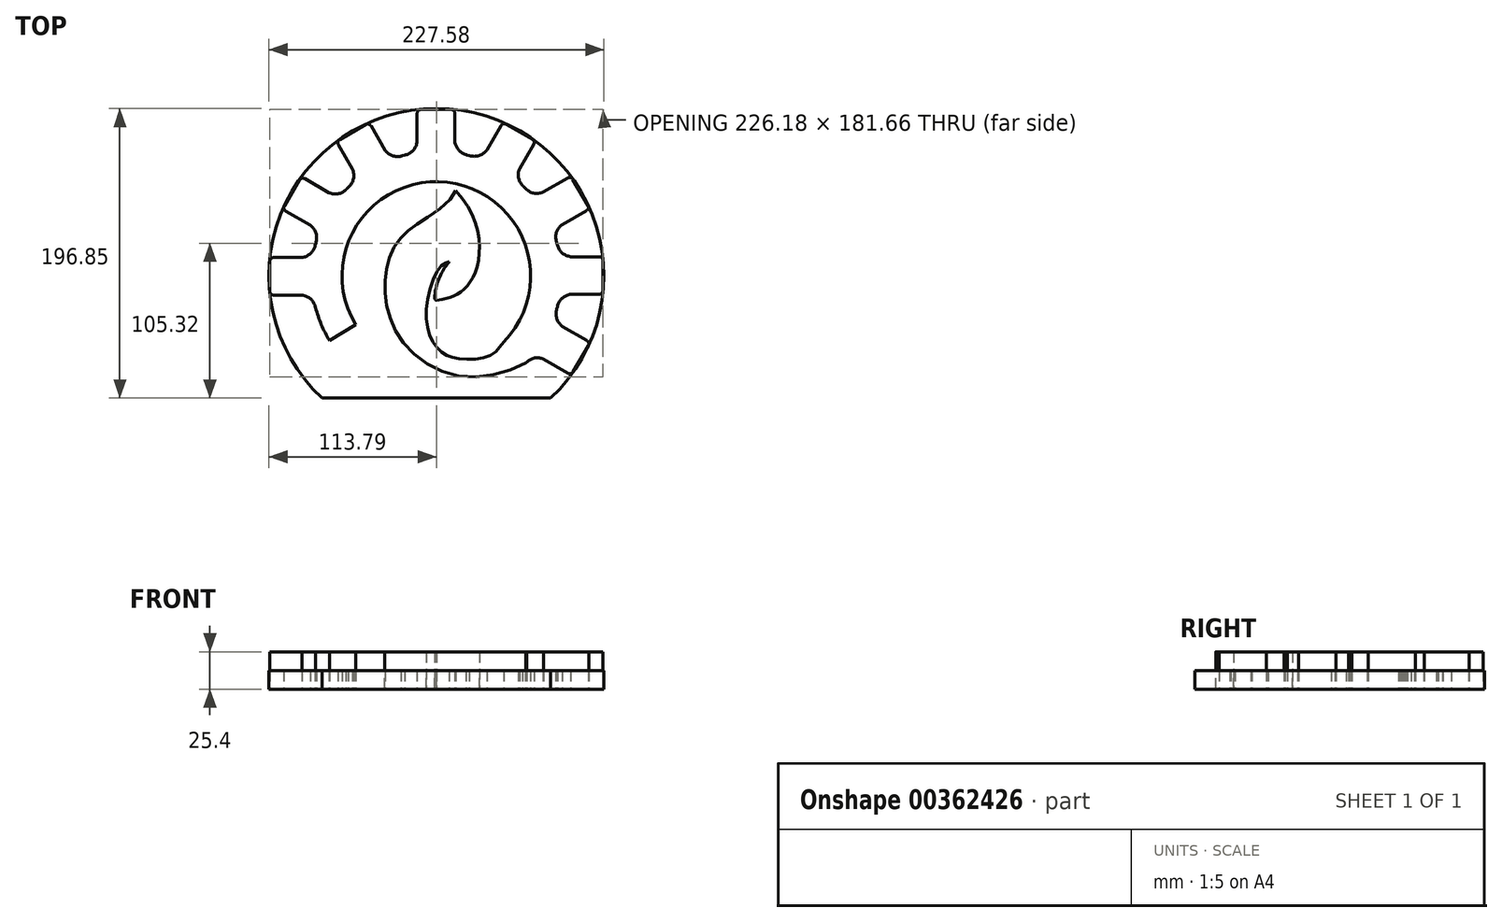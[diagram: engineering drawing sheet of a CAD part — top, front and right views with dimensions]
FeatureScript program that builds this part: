
annotation { "Feature Type Name" : "Feature", "Feature Type Description" : "" }
export const myFeature = defineFeature(function(context is Context, id is Id, definition is map)
    precondition{}
    {
        {
            var Q0;
            Q0=qCreatedBy(makeId("Top.planeOp"),FACE);
            var sketch = newSketch(context, id + "F0", { "sketchPlane" : qUnion([Q0])});
            skArc(sketch, "E0", {"start": v(45.83, -44.78) * mm, "mid": v(7.38, 63.65) * mm, "end": v(-54.86, -33.1) * mm});
            skArc(sketch, "E1", {"start": v(60.8, -59.24) * mm, "mid": v(61.11, -58.91) * mm, "end": v(61.43, -58.58) * mm});
            skLineSegment(sketch, "E2", {"start": v(-91.4, -13.07) * mm, "end": v(-110.55, -13.07) * mm});
            skLineSegment(sketch, "E3", {"start": v(-113.1, -10.53) * mm, "end": v(-113.1, 9.96) * mm});
            skLineSegment(sketch, "E4", {"start": v(-110.55, 12.5) * mm, "end": v(-91.4, 12.5) * mm});
            skPoint(sketch, "E5.visualSharp", {"position": v(-113.1, 12.5) * mm});
            skArc(sketch, "E5.filletArc", {"start": v(-110.55, 12.5) * mm, "mid": v(-112.35, 11.76) * mm, "end": v(-113.1, 9.96) * mm});
            skPoint(sketch, "E6.visualSharp", {"position": v(-113.1, -13.07) * mm});
            skArc(sketch, "E6.filletArc", {"start": v(-113.1, -10.53) * mm, "mid": v(-112.35, -12.32) * mm, "end": v(-110.55, -13.07) * mm});
            skArc(sketch, "E7", {"start": v(-91.4, 12.5) * mm, "mid": v(-85.48, 15.23) * mm, "end": v(-82.27, 20.9) * mm});
            skArc(sketch, "E8.MirrorCS", {"start": v(-91.4, -13.07) * mm, "mid": v(-85.34, -15.78) * mm, "end": v(-82.1, -21.58) * mm});
            skPoint(sketch, "E9.start.orphan", {"position": v(-113.1, -0.28) * mm});
            skArc(sketch, "E10.5.0", {"start": v(72.9, -56.53) * mm, "mid": v(66.41, -55.92) * mm, "end": v(60.8, -59.24) * mm});
            skLineSegment(sketch, "E10.5.1", {"start": v(89.49, -66.1) * mm, "end": v(72.9, -56.53) * mm});
            skLineSegment(sketch, "E10.5.2", {"start": v(103.2, -47.43) * mm, "end": v(92.96, -65.18) * mm});
            skLineSegment(sketch, "E10.5.3", {"start": v(85.69, -34.38) * mm, "end": v(102.27, -43.96) * mm});
            skArc(sketch, "E10.5.4", {"start": v(85.69, -34.38) * mm, "mid": v(81.8, -29) * mm, "end": v(81.89, -22.36) * mm});
            skArc(sketch, "E10.5.5", {"start": v(103.2, -47.43) * mm, "mid": v(103.46, -45.5) * mm, "end": v(102.27, -43.96) * mm});
            skArc(sketch, "E10.5.6", {"start": v(89.49, -66.1) * mm, "mid": v(91.42, -66.36) * mm, "end": v(92.96, -65.18) * mm});
            skArc(sketch, "E10.6.0", {"start": v(91.4, -12.5) * mm, "mid": v(85.48, -15.23) * mm, "end": v(82.27, -20.9) * mm});
            skLineSegment(sketch, "E10.6.1", {"start": v(110.55, -12.5) * mm, "end": v(91.4, -12.5) * mm});
            skLineSegment(sketch, "E10.6.2", {"start": v(113.1, 10.53) * mm, "end": v(113.1, -9.96) * mm});
            skLineSegment(sketch, "E10.6.3", {"start": v(91.4, 13.07) * mm, "end": v(110.55, 13.07) * mm});
            skArc(sketch, "E10.6.4", {"start": v(91.4, 13.07) * mm, "mid": v(85.34, 15.78) * mm, "end": v(82.1, 21.58) * mm});
            skArc(sketch, "E10.6.5", {"start": v(113.1, 10.53) * mm, "mid": v(112.35, 12.32) * mm, "end": v(110.55, 13.07) * mm});
            skArc(sketch, "E10.6.6", {"start": v(110.55, -12.5) * mm, "mid": v(112.35, -11.76) * mm, "end": v(113.1, -9.96) * mm});
            skArc(sketch, "E10.7.0", {"start": v(85.41, 34.87) * mm, "mid": v(81.64, 29.55) * mm, "end": v(81.7, 23.03) * mm});
            skLineSegment(sketch, "E10.7.1", {"start": v(102, 44.45) * mm, "end": v(85.41, 34.87) * mm});
            skLineSegment(sketch, "E10.7.2", {"start": v(92.68, 65.66) * mm, "end": v(102.92, 47.92) * mm});
            skLineSegment(sketch, "E10.7.3", {"start": v(72.62, 57.01) * mm, "end": v(89.2, 66.6) * mm});
            skArc(sketch, "E10.7.4", {"start": v(72.62, 57.01) * mm, "mid": v(66.01, 56.34) * mm, "end": v(60.3, 59.74) * mm});
            skArc(sketch, "E10.7.5", {"start": v(92.68, 65.66) * mm, "mid": v(91.14, 66.84) * mm, "end": v(89.2, 66.6) * mm});
            skArc(sketch, "E10.7.6", {"start": v(102, 44.45) * mm, "mid": v(103.18, 45.99) * mm, "end": v(102.92, 47.92) * mm});
            skArc(sketch, "E10.8.0", {"start": v(56.53, 72.9) * mm, "mid": v(55.92, 66.41) * mm, "end": v(59.24, 60.8) * mm});
            skLineSegment(sketch, "E10.8.1", {"start": v(66.1, 89.49) * mm, "end": v(56.53, 72.9) * mm});
            skLineSegment(sketch, "E10.8.2", {"start": v(47.43, 103.2) * mm, "end": v(65.18, 92.96) * mm});
            skLineSegment(sketch, "E10.8.3", {"start": v(34.38, 85.69) * mm, "end": v(43.96, 102.27) * mm});
            skArc(sketch, "E10.8.4", {"start": v(34.38, 85.69) * mm, "mid": v(29, 81.8) * mm, "end": v(22.36, 81.89) * mm});
            skArc(sketch, "E10.8.5", {"start": v(47.43, 103.2) * mm, "mid": v(45.5, 103.46) * mm, "end": v(43.96, 102.27) * mm});
            skArc(sketch, "E10.8.6", {"start": v(66.1, 89.49) * mm, "mid": v(66.36, 91.42) * mm, "end": v(65.18, 92.96) * mm});
            skArc(sketch, "E10.9.0", {"start": v(12.5, 91.4) * mm, "mid": v(15.23, 85.48) * mm, "end": v(20.9, 82.27) * mm});
            skLineSegment(sketch, "E10.9.1", {"start": v(12.5, 110.55) * mm, "end": v(12.5, 91.4) * mm});
            skLineSegment(sketch, "E10.9.2", {"start": v(-10.53, 113.1) * mm, "end": v(9.96, 113.1) * mm});
            skLineSegment(sketch, "E10.9.3", {"start": v(-13.07, 91.4) * mm, "end": v(-13.07, 110.55) * mm});
            skArc(sketch, "E10.9.4", {"start": v(-13.07, 91.4) * mm, "mid": v(-15.78, 85.34) * mm, "end": v(-21.58, 82.1) * mm});
            skArc(sketch, "E10.9.5", {"start": v(-10.53, 113.1) * mm, "mid": v(-12.32, 112.35) * mm, "end": v(-13.07, 110.55) * mm});
            skArc(sketch, "E10.9.6", {"start": v(12.5, 110.55) * mm, "mid": v(11.76, 112.35) * mm, "end": v(9.96, 113.1) * mm});
            skArc(sketch, "E10.10.0", {"start": v(-34.87, 85.41) * mm, "mid": v(-29.55, 81.64) * mm, "end": v(-23.03, 81.7) * mm});
            skLineSegment(sketch, "E10.10.1", {"start": v(-44.45, 102) * mm, "end": v(-34.87, 85.41) * mm});
            skLineSegment(sketch, "E10.10.2", {"start": v(-65.66, 92.68) * mm, "end": v(-47.92, 102.92) * mm});
            skLineSegment(sketch, "E10.10.3", {"start": v(-57.01, 72.62) * mm, "end": v(-66.6, 89.2) * mm});
            skArc(sketch, "E10.10.4", {"start": v(-57.01, 72.62) * mm, "mid": v(-56.34, 66.01) * mm, "end": v(-59.74, 60.3) * mm});
            skArc(sketch, "E10.10.5", {"start": v(-65.66, 92.68) * mm, "mid": v(-66.84, 91.14) * mm, "end": v(-66.6, 89.2) * mm});
            skArc(sketch, "E10.10.6", {"start": v(-44.45, 102) * mm, "mid": v(-45.99, 103.18) * mm, "end": v(-47.92, 102.92) * mm});
            skArc(sketch, "E10.11.0", {"start": v(-72.9, 56.53) * mm, "mid": v(-66.41, 55.92) * mm, "end": v(-60.8, 59.24) * mm});
            skLineSegment(sketch, "E10.11.1", {"start": v(-89.49, 66.1) * mm, "end": v(-72.9, 56.53) * mm});
            skLineSegment(sketch, "E10.11.2", {"start": v(-103.2, 47.43) * mm, "end": v(-92.96, 65.18) * mm});
            skLineSegment(sketch, "E10.11.3", {"start": v(-85.69, 34.38) * mm, "end": v(-102.27, 43.96) * mm});
            skArc(sketch, "E10.11.4", {"start": v(-85.69, 34.38) * mm, "mid": v(-81.8, 29) * mm, "end": v(-81.89, 22.36) * mm});
            skArc(sketch, "E10.11.5", {"start": v(-103.2, 47.43) * mm, "mid": v(-103.46, 45.5) * mm, "end": v(-102.27, 43.96) * mm});
            skArc(sketch, "E10.11.6", {"start": v(-89.49, 66.1) * mm, "mid": v(-91.42, 66.36) * mm, "end": v(-92.96, 65.18) * mm});
            skLineSegment(sketch, "E11", {"start": v(-72.57, -44.03) * mm, "end": v(-54.86, -33.1) * mm});
            skFitSpline(sketch, "E12", {"points": [v(45.83, -44.78) * mm, v(36.87, -54.1) * mm, v(17.42, -56.49) * mm, v(5.14, -52.9) * mm, v(-3.83, -41.82) * mm, v(-6.23, -17.88) * mm, v(3.2, 6.6) * mm, v(8.72, 9.76) * mm], "startDerivative": vector(-65.05, -82.43) * mm, "endDerivative": vector(42.67, 26.46) * mm});
            skFitSpline(sketch, "E13", {"points": [v(8.72, 9.76) * mm, v(5.03, 4.5) * mm, v(0, -7.07) * mm, v(-0.53, -16.53) * mm, v(0, -16.53) * mm], "startDerivative": vector(-10, -13.85) * mm, "endDerivative": vector(-0.44, -2.73) * mm});
            skFitSpline(sketch, "E14", {"points": [v(0, -16.53) * mm, v(11.97, -13.45) * mm, v(26.25, 2.1) * mm, v(13.23, 57.96) * mm], "startDerivative": vector(39.13, 4.62) * mm, "endDerivative": vector(-112.97, 121.05) * mm});
            skFitSpline(sketch, "E15", {"points": [v(13.23, 57.96) * mm, v(-6.93, 39.06) * mm, v(-24.15, 26.04) * mm, v(-33.39, 7.14) * mm, v(-34.23, -16.8) * mm, v(-22.89, -44.95) * mm, v(13.23, -67.63) * mm, v(60.8, -59.24) * mm], "startDerivative": vector(-43.18, -130.27) * mm, "endDerivative": vector(222.95, 123.76) * mm});
            skArc(sketch, "E16.trimOffspring", {"start": v(82.27, -20.9) * mm, "mid": v(82.38, -20.46) * mm, "end": v(82.49, -20.02) * mm});
            skArc(sketch, "E17.trimOffspring", {"start": v(81.7, 23.03) * mm, "mid": v(81.58, 23.47) * mm, "end": v(81.45, 23.9) * mm});
            skArc(sketch, "E18.trimOffspring", {"start": v(59.24, 60.8) * mm, "mid": v(58.91, 61.11) * mm, "end": v(58.58, 61.43) * mm});
            skArc(sketch, "E19.trimOffspring", {"start": v(20.9, 82.27) * mm, "mid": v(20.46, 82.38) * mm, "end": v(20.02, 82.49) * mm});
            skArc(sketch, "E20.trimOffspring", {"start": v(-23.03, 81.7) * mm, "mid": v(-23.47, 81.58) * mm, "end": v(-23.9, 81.45) * mm});
            skArc(sketch, "E21.trimOffspring", {"start": v(-60.8, 59.24) * mm, "mid": v(-61.11, 58.91) * mm, "end": v(-61.43, 58.58) * mm});
            skArc(sketch, "E22.trimOffspring", {"start": v(-82.27, 20.9) * mm, "mid": v(-82.38, 20.46) * mm, "end": v(-82.49, 20.02) * mm});
            skArc(sketch, "E23.trimOffspring", {"start": v(-82.4, -20.38) * mm, "mid": v(-78.38, -32.58) * mm, "end": v(-72.57, -44.03) * mm});
            skLineSegment(sketch, "E24", {"start": v(-82.27, 20.9) * mm, "end": v(-81.89, 22.36) * mm});
            skLineSegment(sketch, "E25", {"start": v(-60.8, 59.24) * mm, "end": v(-59.74, 60.3) * mm});
            skLineSegment(sketch, "E26", {"start": v(-21.58, 82.1) * mm, "end": v(-23.03, 81.7) * mm});
            skLineSegment(sketch, "E27", {"start": v(22.36, 81.89) * mm, "end": v(20.9, 82.27) * mm});
            skLineSegment(sketch, "E28", {"start": v(60.3, 59.74) * mm, "end": v(59.24, 60.8) * mm});
            skLineSegment(sketch, "E29", {"start": v(82.1, 21.58) * mm, "end": v(81.7, 23.03) * mm});
            skLineSegment(sketch, "E30", {"start": v(81.89, -22.36) * mm, "end": v(82.27, -20.9) * mm});
            skSolve(sketch);
        }
        {
            var Q0;
            {var subQ0=sQuery(id+"F0.wireOp",EDGE,"E1");Q0=makeQuery(id+"F0.imprint","IMPRINT",FACE,{"disambiguationData":[TD([[makeQuery(id+"F0.imprint","IMPRINT",EDGE,{"derivedFrom":subQ0}),1.0]])]});}
            var Q1;
            {var subQ0=sQuery(id+"F0.wireOp",EDGE,"E22.trimOffspring");Q1=makeQuery(id+"F0.imprint","IMPRINT",FACE,{"disambiguationData":[TD([[makeQuery(id+"F0.imprint","IMPRINT",EDGE,{"derivedFrom":subQ0}),1.0]])]});}
            var Q2;
            {var subQ0=sQuery(id+"F0.wireOp",EDGE,"E23.trimOffspring");var subQ1=sQuery(id+"F0.wireOp",EDGE,"E8.MirrorCS");var subQ2=makeQuery(id+"F0.imprint","INTERSECT",VERTEX,{"disambiguationData":[OD(0.0)],"derivedFrom":[subQ1,subQ0]});Q2=makeQuery(id+"F0.imprint","IMPRINT",FACE,{"disambiguationData":[TD([[makeQuery(id+"F0.imprint","IMPRINT",EDGE,{"disambiguationData":[TD([[subQ2,1.0]])],"derivedFrom":subQ1}),-1.0]])]});}
            var Q3;
            {var subQ0=sQuery(id+"F0.wireOp",EDGE,"E16.trimOffspring");Q3=makeQuery(id+"F0.imprint","IMPRINT",FACE,{"disambiguationData":[TD([[makeQuery(id+"F0.imprint","IMPRINT",EDGE,{"derivedFrom":subQ0}),1.0]])]});}
            var Q4;
            {var subQ0=sQuery(id+"F0.wireOp",EDGE,"E17.trimOffspring");Q4=makeQuery(id+"F0.imprint","IMPRINT",FACE,{"disambiguationData":[TD([[makeQuery(id+"F0.imprint","IMPRINT",EDGE,{"derivedFrom":subQ0}),1.0]])]});}
            var Q5;
            {var subQ0=sQuery(id+"F0.wireOp",EDGE,"E18.trimOffspring");Q5=makeQuery(id+"F0.imprint","IMPRINT",FACE,{"disambiguationData":[TD([[makeQuery(id+"F0.imprint","IMPRINT",EDGE,{"derivedFrom":subQ0}),1.0]])]});}
            var Q6;
            {var subQ0=sQuery(id+"F0.wireOp",EDGE,"E19.trimOffspring");Q6=makeQuery(id+"F0.imprint","IMPRINT",FACE,{"disambiguationData":[TD([[makeQuery(id+"F0.imprint","IMPRINT",EDGE,{"derivedFrom":subQ0}),1.0]])]});}
            var Q7;
            {var subQ0=sQuery(id+"F0.wireOp",EDGE,"E20.trimOffspring");Q7=makeQuery(id+"F0.imprint","IMPRINT",FACE,{"disambiguationData":[TD([[makeQuery(id+"F0.imprint","IMPRINT",EDGE,{"derivedFrom":subQ0}),1.0]])]});}
            var Q8;
            {var subQ0=sQuery(id+"F0.wireOp",EDGE,"E21.trimOffspring");Q8=makeQuery(id+"F0.imprint","IMPRINT",FACE,{"disambiguationData":[TD([[makeQuery(id+"F0.imprint","IMPRINT",EDGE,{"derivedFrom":subQ0}),1.0]])]});}
            var Q9;
            {var subQ16=sQuery(id+"F0.wireOp",EDGE,"E2");Q9=makeQuery(id+"F0.imprint","IMPRINT",FACE,{"disambiguationData":[TD([[makeQuery(id+"F0.imprint","IMPRINT",EDGE,{"derivedFrom":subQ16}),-1.0]])]});}
            extrude(context, id + "F1", {"entities" : qUnion([Q0, Q1, Q2, Q3, Q4, Q5, Q6, Q7, Q8, Q9]), "depth" : 25.4 * mm});
        }
        {
            var Q0;
            Q0=makeQuery(id+"F1.opExtrude","CAP_FACE",FACE,{"disambiguationData":[OSD([sQuery(id+"F0.wireOp",EDGE,"E0"),sQuery(id+"F0.wireOp",EDGE,"E1"),sQuery(id+"F0.wireOp",EDGE,"E2"),sQuery(id+"F0.wireOp",EDGE,"E3"),sQuery(id+"F0.wireOp",EDGE,"E4"),sQuery(id+"F0.wireOp",EDGE,"E5.filletArc"),sQuery(id+"F0.wireOp",EDGE,"E6.filletArc"),sQuery(id+"F0.wireOp",EDGE,"E7"),sQuery(id+"F0.wireOp",EDGE,"E8.MirrorCS"),sQuery(id+"F0.wireOp",EDGE,"E10.5.0"),sQuery(id+"F0.wireOp",EDGE,"E10.5.1"),sQuery(id+"F0.wireOp",EDGE,"E10.5.2"),sQuery(id+"F0.wireOp",EDGE,"E10.5.3"),sQuery(id+"F0.wireOp",EDGE,"E10.5.4"),sQuery(id+"F0.wireOp",EDGE,"E10.5.5"),sQuery(id+"F0.wireOp",EDGE,"E10.5.6"),sQuery(id+"F0.wireOp",EDGE,"E10.6.0"),sQuery(id+"F0.wireOp",EDGE,"E10.6.1"),sQuery(id+"F0.wireOp",EDGE,"E10.6.2"),sQuery(id+"F0.wireOp",EDGE,"E10.6.3"),sQuery(id+"F0.wireOp",EDGE,"E10.6.4"),sQuery(id+"F0.wireOp",EDGE,"E10.6.5"),sQuery(id+"F0.wireOp",EDGE,"E10.6.6"),sQuery(id+"F0.wireOp",EDGE,"E10.7.0"),sQuery(id+"F0.wireOp",EDGE,"E10.7.1"),sQuery(id+"F0.wireOp",EDGE,"E10.7.2"),sQuery(id+"F0.wireOp",EDGE,"E10.7.3"),sQuery(id+"F0.wireOp",EDGE,"E10.7.4"),sQuery(id+"F0.wireOp",EDGE,"E10.7.5"),sQuery(id+"F0.wireOp",EDGE,"E10.7.6"),sQuery(id+"F0.wireOp",EDGE,"E10.8.0"),sQuery(id+"F0.wireOp",EDGE,"E10.8.1"),sQuery(id+"F0.wireOp",EDGE,"E10.8.2"),sQuery(id+"F0.wireOp",EDGE,"E10.8.3"),sQuery(id+"F0.wireOp",EDGE,"E10.8.4"),sQuery(id+"F0.wireOp",EDGE,"E10.8.5"),sQuery(id+"F0.wireOp",EDGE,"E10.8.6"),sQuery(id+"F0.wireOp",EDGE,"E10.9.0"),sQuery(id+"F0.wireOp",EDGE,"E10.9.1"),sQuery(id+"F0.wireOp",EDGE,"E10.9.2"),sQuery(id+"F0.wireOp",EDGE,"E10.9.3"),sQuery(id+"F0.wireOp",EDGE,"E10.9.4"),sQuery(id+"F0.wireOp",EDGE,"E10.9.5"),sQuery(id+"F0.wireOp",EDGE,"E10.9.6"),sQuery(id+"F0.wireOp",EDGE,"E10.10.0"),sQuery(id+"F0.wireOp",EDGE,"E10.10.1"),sQuery(id+"F0.wireOp",EDGE,"E10.10.2"),sQuery(id+"F0.wireOp",EDGE,"E10.10.3"),sQuery(id+"F0.wireOp",EDGE,"E10.10.4"),sQuery(id+"F0.wireOp",EDGE,"E10.10.5"),sQuery(id+"F0.wireOp",EDGE,"E10.10.6"),sQuery(id+"F0.wireOp",EDGE,"E10.11.0"),sQuery(id+"F0.wireOp",EDGE,"E10.11.1"),sQuery(id+"F0.wireOp",EDGE,"E10.11.2"),sQuery(id+"F0.wireOp",EDGE,"E10.11.3"),sQuery(id+"F0.wireOp",EDGE,"E10.11.4"),sQuery(id+"F0.wireOp",EDGE,"E10.11.5"),sQuery(id+"F0.wireOp",EDGE,"E10.11.6"),sQuery(id+"F0.wireOp",EDGE,"E11"),sQuery(id+"F0.wireOp",EDGE,"E12"),sQuery(id+"F0.wireOp",EDGE,"E13"),sQuery(id+"F0.wireOp",EDGE,"E14"),sQuery(id+"F0.wireOp",EDGE,"E15"),sQuery(id+"F0.wireOp",EDGE,"E16.trimOffspring"),sQuery(id+"F0.wireOp",EDGE,"E17.trimOffspring"),sQuery(id+"F0.wireOp",EDGE,"E18.trimOffspring"),sQuery(id+"F0.wireOp",EDGE,"E19.trimOffspring"),sQuery(id+"F0.wireOp",EDGE,"E20.trimOffspring"),sQuery(id+"F0.wireOp",EDGE,"E21.trimOffspring"),sQuery(id+"F0.wireOp",EDGE,"E22.trimOffspring"),sQuery(id+"F0.wireOp",EDGE,"E23.trimOffspring"),sQuery(id+"F0.wireOp",EDGE,"E24"),sQuery(id+"F0.wireOp",EDGE,"E25"),sQuery(id+"F0.wireOp",EDGE,"E26"),sQuery(id+"F0.wireOp",EDGE,"E27"),sQuery(id+"F0.wireOp",EDGE,"E28"),sQuery(id+"F0.wireOp",EDGE,"E29"),sQuery(id+"F0.wireOp",EDGE,"E30")])],"isStart":true});
            var sketch = newSketch(context, id + "F2", { "sketchPlane" : qUnion([Q0])});
            skCircle(sketch, "E31", {"center": v(0, 0) * mm, "radius": 113.79 * mm});
            skSolve(sketch);
        }
        {
            var Q0;
            Q0=makeQuery(id+"F2.imprint","IMPRINT",FACE,{"disambiguationData":[TD([[makeQuery(id+"F2.imprint","IMPRINT",EDGE,{"derivedFrom":sQuery(id+"F2.wireOp",EDGE,"E31")}),1.0]])]});
            extrude(context, id + "F3", {"entities" : qUnion([Q0]), "oppositeDirection" : true, "depth" : 12.7 * mm});
        }
        {
            var Q0;
            Q0=makeQuery(id+"F3.opExtrude","CAP_FACE",FACE,{"disambiguationData":[OSD([sQuery(id+"F0.wireOp",EDGE,"E0"),sQuery(id+"F0.wireOp",EDGE,"E1"),sQuery(id+"F0.wireOp",EDGE,"E2"),sQuery(id+"F0.wireOp",EDGE,"E3"),sQuery(id+"F0.wireOp",EDGE,"E4"),sQuery(id+"F0.wireOp",EDGE,"E5.filletArc"),sQuery(id+"F0.wireOp",EDGE,"E6.filletArc"),sQuery(id+"F0.wireOp",EDGE,"E7"),sQuery(id+"F0.wireOp",EDGE,"E8.MirrorCS"),sQuery(id+"F0.wireOp",EDGE,"E10.5.0"),sQuery(id+"F0.wireOp",EDGE,"E10.5.1"),sQuery(id+"F0.wireOp",EDGE,"E10.5.2"),sQuery(id+"F0.wireOp",EDGE,"E10.5.3"),sQuery(id+"F0.wireOp",EDGE,"E10.5.4"),sQuery(id+"F0.wireOp",EDGE,"E10.5.5"),sQuery(id+"F0.wireOp",EDGE,"E10.5.6"),sQuery(id+"F0.wireOp",EDGE,"E10.6.0"),sQuery(id+"F0.wireOp",EDGE,"E10.6.1"),sQuery(id+"F0.wireOp",EDGE,"E10.6.2"),sQuery(id+"F0.wireOp",EDGE,"E10.6.3"),sQuery(id+"F0.wireOp",EDGE,"E10.6.4"),sQuery(id+"F0.wireOp",EDGE,"E10.6.5"),sQuery(id+"F0.wireOp",EDGE,"E10.6.6"),sQuery(id+"F0.wireOp",EDGE,"E10.7.0"),sQuery(id+"F0.wireOp",EDGE,"E10.7.1"),sQuery(id+"F0.wireOp",EDGE,"E10.7.2"),sQuery(id+"F0.wireOp",EDGE,"E10.7.3"),sQuery(id+"F0.wireOp",EDGE,"E10.7.4"),sQuery(id+"F0.wireOp",EDGE,"E10.7.5"),sQuery(id+"F0.wireOp",EDGE,"E10.7.6"),sQuery(id+"F0.wireOp",EDGE,"E10.8.0"),sQuery(id+"F0.wireOp",EDGE,"E10.8.1"),sQuery(id+"F0.wireOp",EDGE,"E10.8.2"),sQuery(id+"F0.wireOp",EDGE,"E10.8.3"),sQuery(id+"F0.wireOp",EDGE,"E10.8.4"),sQuery(id+"F0.wireOp",EDGE,"E10.8.5"),sQuery(id+"F0.wireOp",EDGE,"E10.8.6"),sQuery(id+"F0.wireOp",EDGE,"E10.9.0"),sQuery(id+"F0.wireOp",EDGE,"E10.9.1"),sQuery(id+"F0.wireOp",EDGE,"E10.9.2"),sQuery(id+"F0.wireOp",EDGE,"E10.9.3"),sQuery(id+"F0.wireOp",EDGE,"E10.9.4"),sQuery(id+"F0.wireOp",EDGE,"E10.9.5"),sQuery(id+"F0.wireOp",EDGE,"E10.9.6"),sQuery(id+"F0.wireOp",EDGE,"E10.10.0"),sQuery(id+"F0.wireOp",EDGE,"E10.10.1"),sQuery(id+"F0.wireOp",EDGE,"E10.10.2"),sQuery(id+"F0.wireOp",EDGE,"E10.10.3"),sQuery(id+"F0.wireOp",EDGE,"E10.10.4"),sQuery(id+"F0.wireOp",EDGE,"E10.10.5"),sQuery(id+"F0.wireOp",EDGE,"E10.10.6"),sQuery(id+"F0.wireOp",EDGE,"E10.11.0"),sQuery(id+"F0.wireOp",EDGE,"E10.11.1"),sQuery(id+"F0.wireOp",EDGE,"E10.11.2"),sQuery(id+"F0.wireOp",EDGE,"E10.11.3"),sQuery(id+"F0.wireOp",EDGE,"E10.11.4"),sQuery(id+"F0.wireOp",EDGE,"E10.11.5"),sQuery(id+"F0.wireOp",EDGE,"E10.11.6"),sQuery(id+"F0.wireOp",EDGE,"E11"),sQuery(id+"F0.wireOp",EDGE,"E12"),sQuery(id+"F0.wireOp",EDGE,"E13"),sQuery(id+"F0.wireOp",EDGE,"E14"),sQuery(id+"F0.wireOp",EDGE,"E15"),sQuery(id+"F0.wireOp",EDGE,"E16.trimOffspring"),sQuery(id+"F0.wireOp",EDGE,"E17.trimOffspring"),sQuery(id+"F0.wireOp",EDGE,"E18.trimOffspring"),sQuery(id+"F0.wireOp",EDGE,"E19.trimOffspring"),sQuery(id+"F0.wireOp",EDGE,"E20.trimOffspring"),sQuery(id+"F0.wireOp",EDGE,"E21.trimOffspring"),sQuery(id+"F0.wireOp",EDGE,"E22.trimOffspring"),sQuery(id+"F0.wireOp",EDGE,"E23.trimOffspring"),sQuery(id+"F0.wireOp",EDGE,"E24"),sQuery(id+"F0.wireOp",EDGE,"E25"),sQuery(id+"F0.wireOp",EDGE,"E26"),sQuery(id+"F0.wireOp",EDGE,"E27"),sQuery(id+"F0.wireOp",EDGE,"E28"),sQuery(id+"F0.wireOp",EDGE,"E29"),sQuery(id+"F0.wireOp",EDGE,"E30"),sQuery(id+"F2.wireOp",EDGE,"E31")])],"isStart":false});
            var sketch = newSketch(context, id + "F4", { "sketchPlane" : qUnion([Q0])});
            skLineSegment(sketch, "E32", {"start": v(-77.78, -83.06) * mm, "end": v(77.78, -83.06) * mm});
            skSolve(sketch);
        }
        {
            var Q0;
            Q0 = qSketchRegion(id + "F4", true);
            var Q1;
            {var subQ0=sQuery(id+"F4.wireOp",EDGE,"E32");Q1=makeQuery(id+"F4.imprint","IMPRINT",FACE,{"disambiguationData":[TD([[makeQuery(id+"F4.imprint","IMPRINT",EDGE,{"derivedFrom":subQ0}),-1.0]])]});}
            extrude(context, id + "F5", {"entities" : qUnion([Q0, Q1]), "operationType" : NewBodyOperationType.REMOVE, "oppositeDirection" : true, "depth" : 25.4 * mm});
        }
    });
